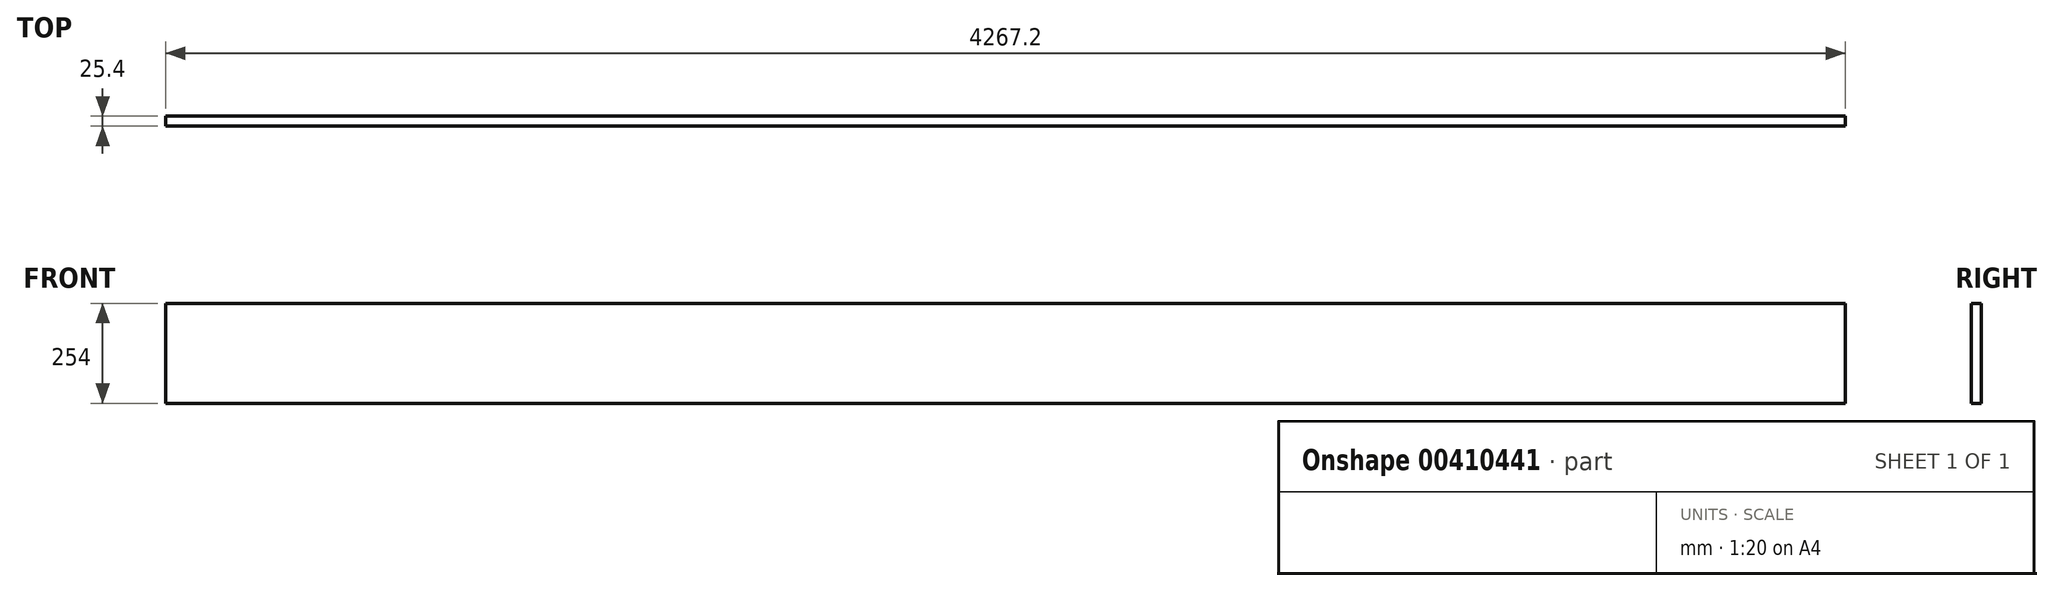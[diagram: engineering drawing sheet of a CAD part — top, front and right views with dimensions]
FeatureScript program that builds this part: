
annotation { "Feature Type Name" : "Feature", "Feature Type Description" : "" }
export const myFeature = defineFeature(function(context is Context, id is Id, definition is map)
    precondition{}
    {
        {
            var Q0;
            Q0=qCreatedBy(makeId("Front.planeOp"),FACE);
            var sketch = newSketch(context, id + "F0", { "sketchPlane" : qUnion([Q0])});
            skLineSegment(sketch, "E0.bottom", {"start": v(-2133.6, 127) * mm, "end": v(2133.6, 127) * mm});
            skLineSegment(sketch, "E0.top", {"start": v(-2133.6, -127) * mm, "end": v(2133.6, -127) * mm});
            skLineSegment(sketch, "E0.left", {"start": v(-2133.6, 127) * mm, "end": v(-2133.6, -127) * mm});
            skLineSegment(sketch, "E0.right", {"start": v(2133.6, 127) * mm, "end": v(2133.6, -127) * mm});
            skPoint(sketch, "E0.middle", {"position": v(0, 0) * mm});
            skSolve(sketch);
        }
        {
            var Q0;
            Q0=qSketchRegion(id+"F0",true);
            extrude(context, id + "F1", {"entities" : qUnion([Q0]), "depth" : 25.4 * mm, "offsetDistance" : 25.4 * mm});
        }
    });
